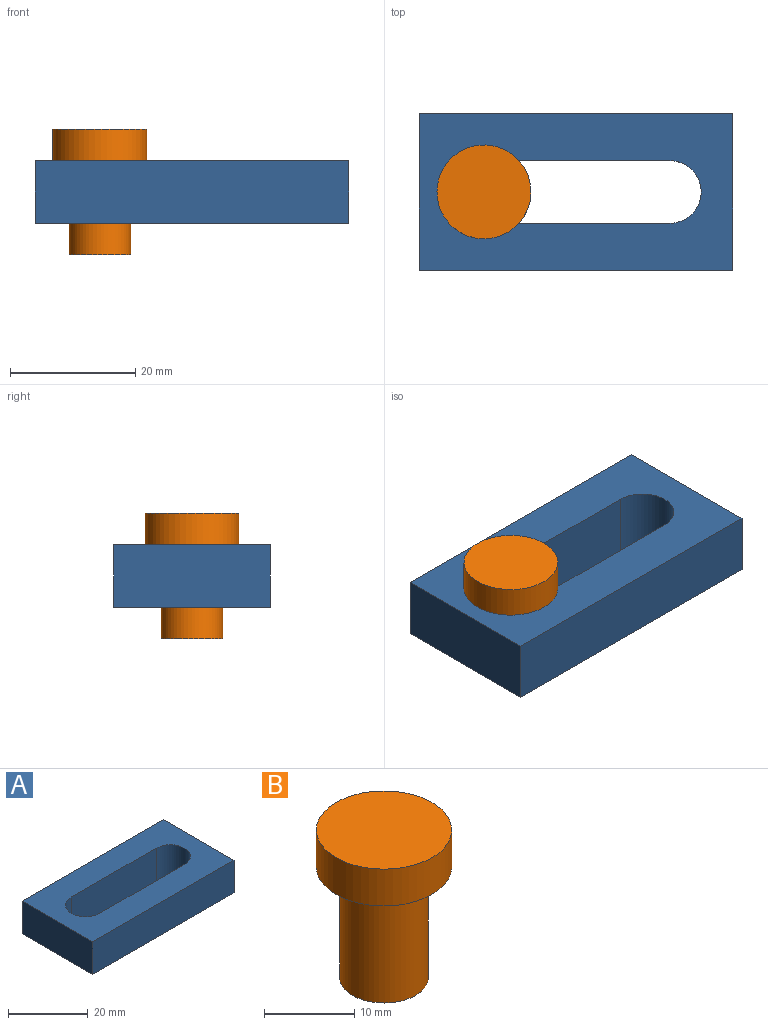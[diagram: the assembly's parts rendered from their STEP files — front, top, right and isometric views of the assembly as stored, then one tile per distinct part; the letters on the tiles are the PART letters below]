
ASSEMBLY  parts=2 mates=1
PART A: 10 faces, bbox 50x25x10 mm
  f0: plane 50x25mm, normal (0,0,1), area 871.5mm2, adj f2,f3,f4,f5,f6,f7,f8,f9
  f1: plane 50x25mm, normal (0,0,-1), area 871.5mm2, adj f2,f3,f4,f5,f6,f7,f8,f9
  f2: plane 50x10mm, normal (0,-1,0), area 500mm2, adj f0,f1,f3,f5
  f3: plane 25x10mm, normal (1,0,0), area 250mm2, adj f0,f1,f2,f4
  f4: plane 50x10mm, normal (0,1,0), area 500mm2, adj f0,f1,f3,f5
  f5: plane 25x10mm, normal (-1,0,0), area 250mm2, adj f0,f1,f2,f4
  f6: plane 30x10mm, normal (0,1,0), area 300mm2, adj f0,f1,f7,f9
  f7: cylinder r=5mm len=10mm, axis (0,0,1), area 157.1mm2, adj f0,f1,f6,f8
  f8: plane 30x10mm, normal (0,-1,0), area 300mm2, adj f0,f1,f7,f9
  f9: cylinder r=5mm len=10mm, axis (0,0,1), area 157.1mm2, adj f0,f1,f6,f8
PART B: 5 faces, bbox 15x15x20 mm
  f0: cylinder r=4.9mm len=15mm, axis (0,0,-1), area 461.8mm2, adj f1,f4
  f1: plane 9.8x9.8mm, normal (0,0,-1), area 75.4mm2, adj f0
  f2: cylinder r=7.5mm len=15mm, axis (0,0,-1), area 235.6mm2, adj f3,f4
  f3: plane 15x15mm, normal (0,0,1), area 176.7mm2, adj f2
  f4: plane 15x15mm, normal (0,0,-1), area 101.3mm2, adj f0,f2
PLACE A at identity fixed
PLACE B rot(axis=(0,0,1),115.9deg) t=(-14.7,0,-5)mm
MATE pin_slot B.f0 <-> A.f0  axis (0,0,-1) through (-14.7,0,10)mm
